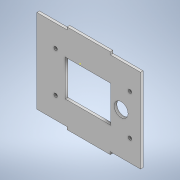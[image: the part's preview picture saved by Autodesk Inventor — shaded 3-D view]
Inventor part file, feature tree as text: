
AUTODESK INVENTOR PART (.ipt)
format: ipt  version: 2020 (Build 240168000, 168)  size: 163,328 bytes
history: native  units: in
note: dims shown in document units (in); Inventor stores cm internally (conversion verified against a paired STEP export)
features: sketch x7, extrude x4
ambient origin geometry x8: Origin, YZ Plane, XZ Plane, XY Plane, X Axis, Y Axis, Z Axis, Center Point
bodies: Solid1 (feature_tree)
feature tree (11):
  extrude  "Extrusion1"  Depth=1.9685in
  extrude  "Extrusion2"  Depth=1.378in
  extrude  "Extrusion3"  Depth=3.8189in
  extrude  "Extrusion4"  Depth=1.378in
  sketch  "Sketch6"  dims[d8=1.9685in]
  sketch  "Sketch7"  dims[d9=1.378in]
  sketch  "Sketch8"  dims[d10=0.1181in d11=0.0in d30=0.1575in d34=0.1575in d35=0.1575in d36=0.1575in d38=0.5512in d43=2.0039in d44=1.5748in d49=0.3937in d50=0.0in d51=0.3937in d52=0.0in d58=0.3937in d59=0.0in d12=0.1969in d13=0.0344in]
  sketch  "Sketch2"  dims[d0=0.1181in d1=1.9685in]
  sketch  "Sketch3"  dims[d2=1.378in d3=1.378in]
  sketch  "Sketch4"  dims[d4=3.8189in d5=3.8189in]
  sketch  "Sketch5"  dims[d6=0.1181in d7=1.378in]
